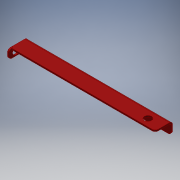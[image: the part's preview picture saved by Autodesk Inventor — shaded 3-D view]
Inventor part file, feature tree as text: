
AUTODESK INVENTOR PART (.ipt)
format: ipt  version: 2018 (Build 220112000, 112)  size: 160,256 bytes
history: native  units: mm
features: other x11, sketch x5, hole x2
ambient origin geometry x8: Origin, YZ Plane, XZ Plane, XY Plane, X Axis, Y Axis, Z Axis, Center Point
bodies: Body1 (feature_tree)
feature tree (18):
  other  "Faccia4"
  other  "Flangia9"
  other  "Flangia10"
  hole  "Foro7"  [1 undecoded]
  other  "Arrotondamento angolo7"
  hole  "Foro9"  [1 undecoded]
  sketch  "Schizzo9"
  other  "Piano6"
  sketch  "Schizzo19"
  other  "Piano13"
  other  "Piega (Bend)9"
  other  "Angolo9"
  sketch  "Schizzo20"
  other  "Piano14"
  other  "Piega (Bend)10"
  other  "Angolo10"
  sketch  "Schizzo21"
  sketch  "Schizzo23"
note: 2 required parameter values undecoded (feature->parameter linkage not recoverable at this tier; creation-order binding heuristic only, values carry confidence <= 0.55)
